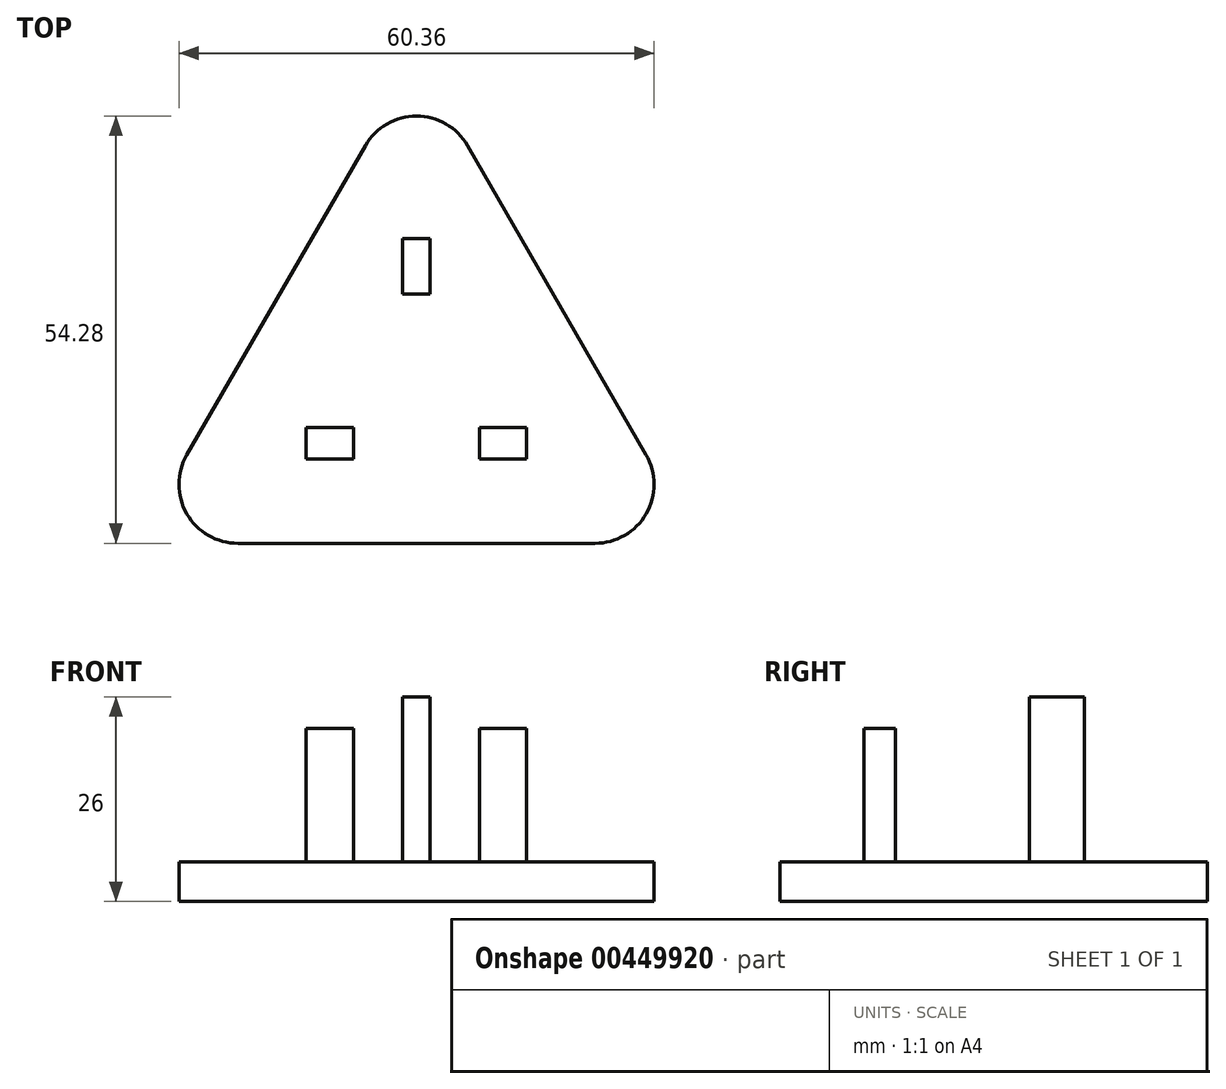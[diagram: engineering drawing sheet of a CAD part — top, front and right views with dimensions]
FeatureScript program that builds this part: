
annotation { "Feature Type Name" : "Feature", "Feature Type Description" : "" }
export const myFeature = defineFeature(function(context is Context, id is Id, definition is map)
    precondition{}
    {
        {
            var Q0;
            Q0=qCreatedBy(makeId("Top.planeOp"),FACE);
            var sketch = newSketch(context, id + "F0", { "sketchPlane" : qUnion([Q0])});
            skCircle(sketch, "E0.cCircle", {"center": v(0, 0) * mm, "radius": 23.1 * mm, "construction": true});
            skLineSegment(sketch, "E0.0", {"start": v(-40, -23.1) * mm, "end": v(0, 46.19) * mm, "construction": true});
            skLineSegment(sketch, "E0.1", {"start": v(0, 46.19) * mm, "end": v(40, -23.1) * mm, "construction": true});
            skLineSegment(sketch, "E0.2", {"start": v(40, -23.1) * mm, "end": v(-40, -23.1) * mm, "construction": true});
            skPoint(sketch, "E0.0.midPoint", {"position": v(-20, 11.55) * mm});
            skLineSegment(sketch, "E1.0", {"start": v(35.67, -20.6) * mm, "end": v(-35.67, -20.6) * mm});
            skLineSegment(sketch, "E1.1", {"start": v(0, 41.19) * mm, "end": v(35.67, -20.6) * mm});
            skLineSegment(sketch, "E1.2", {"start": v(-35.67, -20.6) * mm, "end": v(0, 41.19) * mm});
            skSolve(sketch);
        }
        {
            var Q0;
            Q0=makeQuery(id+"F0.imprint","IMPRINT",FACE,{"disambiguationData":[TD([[makeQuery(id+"F0.imprint","IMPRINT",EDGE,{"derivedFrom":sQuery(id+"F0.wireOp",EDGE,"E1.0")}),-1.0]])]});
            extrude(context, id + "F1", {"entities" : qUnion([Q0]), "depth" : 5 * mm, "offsetDistance" : 25 * mm});
        }
        {
            var Q0;
            Q0=makeQuery(id+"F1.opExtrude","SWEPT_EDGE",EDGE,{"disambiguationData":[OSD([sQuery(id+"F0.wireOp",EDGE,"E1.0"),sQuery(id+"F0.wireOp",EDGE,"E1.1")])]});
            var Q1;
            Q1=makeQuery(id+"F1.opExtrude","SWEPT_EDGE",EDGE,{"disambiguationData":[OSD([sQuery(id+"F0.wireOp",EDGE,"E1.1"),sQuery(id+"F0.wireOp",EDGE,"E1.2")])]});
            var Q2;
            Q2=makeQuery(id+"F1.opExtrude","SWEPT_EDGE",EDGE,{"disambiguationData":[OSD([sQuery(id+"F0.wireOp",EDGE,"E1.0"),sQuery(id+"F0.wireOp",EDGE,"E1.2")])]});
            fillet(context, id + "F2", {"entities" : qUnion([Q0, Q1, Q2]), "radius" : 7.5 * mm, "tangentPropagation" : true, "allowEdgeOverflow" : false});
        }
        {
            var Q0;
            Q0=makeQuery(id+"F1.opExtrude","CAP_FACE",FACE,{"disambiguationData":[OSD([sQuery(id+"F0.wireOp",EDGE,"E1.0"),sQuery(id+"F0.wireOp",EDGE,"E1.1"),sQuery(id+"F0.wireOp",EDGE,"E1.2")])],"isStart":false});
            var sketch = newSketch(context, id + "F3", { "sketchPlane" : qUnion([Q0])});
            skPoint(sketch, "E2.endSnap0", {"position": v(0, -27.9) * mm});
            skLineSegment(sketch, "E3.bottom", {"start": v(-8, -9.9) * mm, "end": v(-14, -9.9) * mm});
            skLineSegment(sketch, "E3.top", {"start": v(-8, -5.9) * mm, "end": v(-14, -5.9) * mm});
            skLineSegment(sketch, "E3.left", {"start": v(-8, -9.9) * mm, "end": v(-8, -5.9) * mm});
            skLineSegment(sketch, "E3.right", {"start": v(-14, -9.9) * mm, "end": v(-14, -5.9) * mm});
            skLineSegment(sketch, "E4.bottom", {"start": v(8, -9.9) * mm, "end": v(14, -9.9) * mm});
            skLineSegment(sketch, "E4.top", {"start": v(8, -5.9) * mm, "end": v(14, -5.9) * mm});
            skLineSegment(sketch, "E4.left", {"start": v(8, -9.9) * mm, "end": v(8, -5.9) * mm});
            skLineSegment(sketch, "E4.right", {"start": v(14, -9.9) * mm, "end": v(14, -5.9) * mm});
            skLineSegment(sketch, "E5", {"start": v(1.75, 11.1) * mm, "end": v(1.75, 18.1) * mm});
            skLineSegment(sketch, "E6", {"start": v(1.75, 18.1) * mm, "end": v(-1.75, 18.1) * mm});
            skLineSegment(sketch, "E7", {"start": v(-1.75, 18.1) * mm, "end": v(-1.75, 11.1) * mm});
            skLineSegment(sketch, "E8", {"start": v(-1.75, 11.1) * mm, "end": v(1.75, 11.1) * mm});
            skSolve(sketch);
        }
        {
            var Q0;
            Q0=makeQuery(id+"F3.imprint","IMPRINT",FACE,{"disambiguationData":[TD([[makeQuery(id+"F3.imprint","IMPRINT",EDGE,{"derivedFrom":sQuery(id+"F3.wireOp",EDGE,"E3.bottom")}),-1.0]])]});
            var Q1;
            Q1=makeQuery(id+"F3.imprint","IMPRINT",FACE,{"disambiguationData":[TD([[makeQuery(id+"F3.imprint","IMPRINT",EDGE,{"derivedFrom":sQuery(id+"F3.wireOp",EDGE,"E4.bottom")}),1.0]])]});
            var Q2;
            Q2=makeQuery(id+"F3.imprint","IMPRINT",FACE,{"disambiguationData":[TD([[makeQuery(id+"F3.imprint","IMPRINT",EDGE,{"derivedFrom":sQuery(id+"F3.wireOp",EDGE,"E5")}),1.0]])]});
            extrude(context, id + "F4", {"entities" : qUnion([Q0, Q1, Q2]), "operationType" : NewBodyOperationType.ADD, "depth" : 17 * mm, "offsetDistance" : 25 * mm});
        }
        {
            var Q0;
            Q0=makeQuery(id+"F4.opExtrude","CAP_FACE",FACE,{"disambiguationData":[OSD([sQuery(id+"F3.wireOp",EDGE,"E5"),sQuery(id+"F3.wireOp",EDGE,"E6"),sQuery(id+"F3.wireOp",EDGE,"E7"),sQuery(id+"F3.wireOp",EDGE,"E8")])],"isStart":false});
            extrude(context, id + "F5", {"entities" : qUnion([Q0]), "operationType" : NewBodyOperationType.ADD, "depth" : 4 * mm, "offsetDistance" : 25 * mm});
        }
    });
